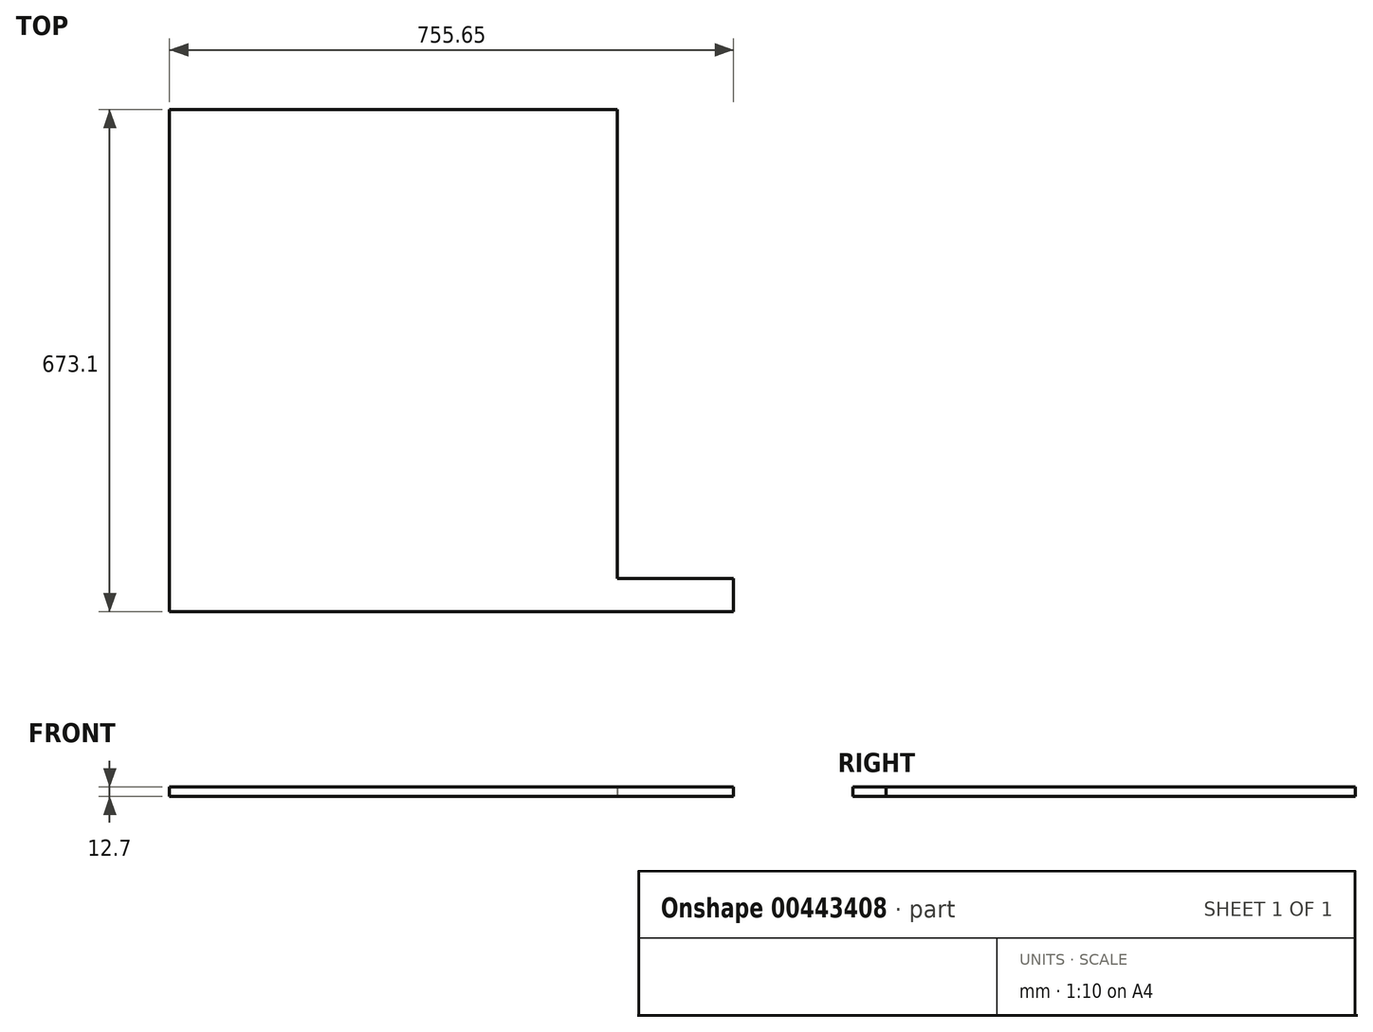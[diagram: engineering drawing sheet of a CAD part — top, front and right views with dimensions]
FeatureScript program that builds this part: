
annotation { "Feature Type Name" : "Feature", "Feature Type Description" : "" }
export const myFeature = defineFeature(function(context is Context, id is Id, definition is map)
    precondition{}
    {
        {
            var Q0;
            Q0=qCreatedBy(makeId("Top.planeOp"),FACE);
            var sketch = newSketch(context, id + "F0", { "sketchPlane" : qUnion([Q0])});
            skLineSegment(sketch, "E0.bottom", {"start": v(-300.04, 336.55) * mm, "end": v(300.04, 336.55) * mm});
            skLineSegment(sketch, "E0.top", {"start": v(-300.04, -336.55) * mm, "end": v(300.04, -336.55) * mm});
            skLineSegment(sketch, "E0.left", {"start": v(-300.04, 336.55) * mm, "end": v(-300.04, -336.55) * mm});
            skLineSegment(sketch, "E0.right", {"start": v(300.04, 336.55) * mm, "end": v(300.04, -292.1) * mm});
            skPoint(sketch, "E0.middle", {"position": v(0, 0) * mm});
            skLineSegment(sketch, "E1.bottom", {"start": v(300.04, -336.55) * mm, "end": v(455.61, -336.55) * mm});
            skLineSegment(sketch, "E1.top", {"start": v(300.04, -292.1) * mm, "end": v(455.61, -292.1) * mm});
            skLineSegment(sketch, "E1.right", {"start": v(455.61, -336.55) * mm, "end": v(455.61, -292.1) * mm});
            skSolve(sketch);
        }
        {
            var Q0;
            Q0 = qSketchRegion(id + "F0", true);
            extrude(context, id + "F1", {"entities" : qUnion([Q0]), "depth" : 12.7 * mm});
        }
    });
